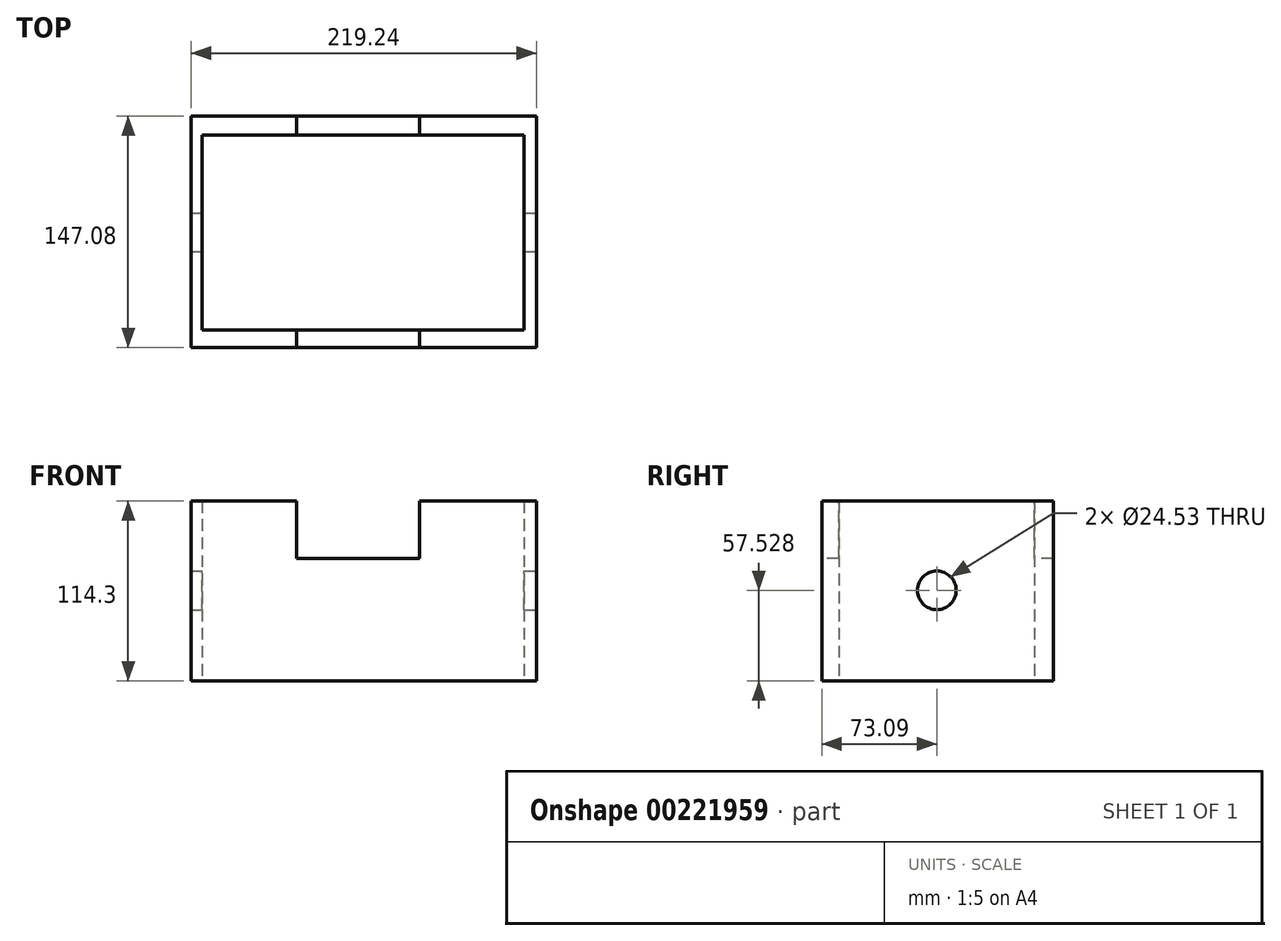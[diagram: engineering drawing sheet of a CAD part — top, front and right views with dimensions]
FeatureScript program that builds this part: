
annotation { "Feature Type Name" : "Feature", "Feature Type Description" : "" }
export const myFeature = defineFeature(function(context is Context, id is Id, definition is map)
    precondition{}
    {
        {
            var Q0;
            Q0=qCreatedBy(makeId("Top.planeOp"),FACE);
            var sketch = newSketch(context, id + "F0", { "sketchPlane" : qUnion([Q0])});
            skLineSegment(sketch, "E0.bottom", {"start": v(-99.42, 74) * mm, "end": v(119.82, 74) * mm});
            skLineSegment(sketch, "E0.top", {"start": v(-99.42, -73.1) * mm, "end": v(119.82, -73.1) * mm});
            skLineSegment(sketch, "E0.left", {"start": v(-99.42, 74) * mm, "end": v(-99.42, -73.1) * mm});
            skLineSegment(sketch, "E0.right", {"start": v(119.82, 74) * mm, "end": v(119.82, -73.1) * mm});
            skSolve(sketch);
        }
        {
            var Q0;
            Q0 = qSketchRegion(id + "F0", true);
            extrude(context, id + "F1", {"entities" : qUnion([Q0]), "depth" : 114.3 * mm});
        }
        {
            var Q0;
            Q0=makeQuery(id+"F1.opExtrude","SWEPT_FACE",FACE,{"disambiguationData":[OSD([sQuery(id+"F0.wireOp",EDGE,"E0.top")])]});
            var sketch = newSketch(context, id + "F2", { "sketchPlane" : qUnion([Q0])});
            skLineSegment(sketch, "E1", {"start": v(-32.64, 114.3) * mm, "end": v(-32.64, 77.79) * mm});
            skLineSegment(sketch, "E2", {"start": v(-32.64, 77.79) * mm, "end": v(45.68, 77.79) * mm});
            skLineSegment(sketch, "E3", {"start": v(45.68, 77.79) * mm, "end": v(45.68, 114.3) * mm});
            skLineSegment(sketch, "E4", {"start": v(45.68, 114.3) * mm, "end": v(-32.64, 114.3) * mm});
            skSolve(sketch);
        }
        {
            var Q0;
            Q0 = qSketchRegion(id + "F2", true);
            extrude(context, id + "F3", {"entities" : qUnion([Q0]), "operationType" : NewBodyOperationType.REMOVE, "endBound" : BoundingType.THROUGH_ALL, "oppositeDirection" : true, "depth" : 25.4 * mm});
        }
        {
            var Q0;
            Q0=makeQuery(id+"F1.opExtrude","CAP_FACE",FACE,{"disambiguationData":[OSD([sQuery(id+"F0.wireOp",EDGE,"E0.bottom"),sQuery(id+"F0.wireOp",EDGE,"E0.top"),sQuery(id+"F0.wireOp",EDGE,"E0.left"),sQuery(id+"F0.wireOp",EDGE,"E0.right")])],"isStart":true});
            var sketch = newSketch(context, id + "F4", { "sketchPlane" : qUnion([Q0])});
            skLineSegment(sketch, "E5.bottom", {"start": v(112.04, -61.83) * mm, "end": v(-92.43, -61.83) * mm});
            skLineSegment(sketch, "E5.top", {"start": v(112.04, 62.12) * mm, "end": v(-92.43, 62.12) * mm});
            skLineSegment(sketch, "E5.left", {"start": v(112.04, -61.83) * mm, "end": v(112.04, 62.12) * mm});
            skLineSegment(sketch, "E5.right", {"start": v(-92.43, -61.83) * mm, "end": v(-92.43, 62.12) * mm});
            skSolve(sketch);
        }
        {
            var Q0;
            Q0 = qSketchRegion(id + "F4", true);
            extrude(context, id + "F5", {"entities" : qUnion([Q0]), "operationType" : NewBodyOperationType.REMOVE, "endBound" : BoundingType.THROUGH_ALL, "oppositeDirection" : true, "depth" : 25.4 * mm});
        }
        {
            var Q0;
            Q0=makeQuery(id+"F1.opExtrude","SWEPT_FACE",FACE,{"disambiguationData":[OSD([sQuery(id+"F0.wireOp",EDGE,"E0.right")])]});
            var sketch = newSketch(context, id + "F6", { "sketchPlane" : qUnion([Q0])});
            skCircle(sketch, "E6", {"center": v(0, 57.53) * mm, "radius": 12.26 * mm});
            skSolve(sketch);
        }
        {
            var Q0;
            Q0 = qSketchRegion(id + "F6", true);
            extrude(context, id + "F7", {"entities" : qUnion([Q0]), "operationType" : NewBodyOperationType.REMOVE, "endBound" : BoundingType.THROUGH_ALL, "oppositeDirection" : true, "depth" : 25.4 * mm});
        }
    });
